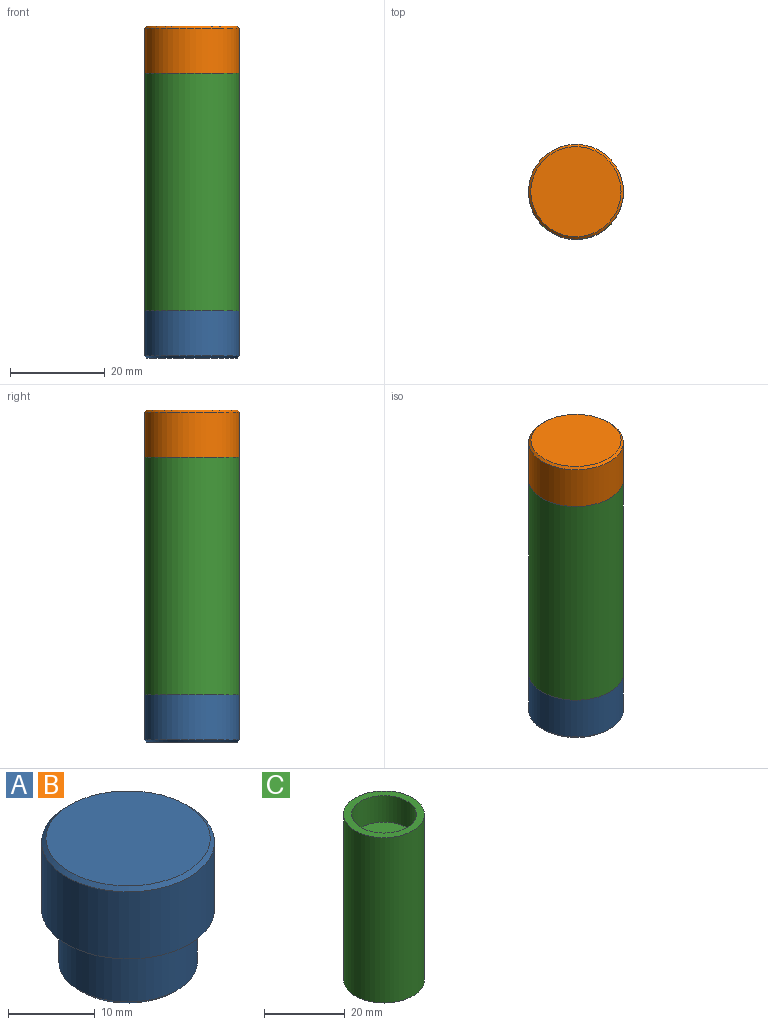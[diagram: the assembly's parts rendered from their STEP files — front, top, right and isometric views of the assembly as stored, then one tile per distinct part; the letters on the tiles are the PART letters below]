
ASSEMBLY  parts=3 mates=2
PART A: 7 faces, bbox 20x20x18 mm
  f0: cylinder r=10mm len=20mm, axis (0,0,-1), area 596.9mm2, adj f2,f6
  f1: plane 19x19mm, normal (0,0,1), area 283.5mm2, adj f6
  f2: plane 20x20mm, normal (0,0,-1), area 113.1mm2, adj f0,f3
  f3: cylinder r=8mm len=16mm, axis (0,0,1), area 377mm2, adj f2,f5
  f4: plane 15x15mm, normal (0,0,-1), area 176.7mm2, adj f5
  f5: cone r=8mm half-angle=45deg, axis (0,0,1), area 34.4mm2, adj f3,f4
  f6: cone r=9.5mm half-angle=45deg, axis (0,0,-1), area 43.3mm2, adj f0,f1
PART B: same geometry as A
PART C: 8 faces, bbox 20x20x50 mm
  f0: cylinder r=2mm len=7mm, axis (0,0,-1), area 88mm2, adj f5,f7
  f1: cylinder r=10mm len=50mm, axis (0,0,-1), area 3141.6mm2, adj f2,f3
  f2: plane 20x20mm, normal (0,0,1), area 113.1mm2, adj f1,f4
  f3: plane 20x20mm, normal (0,0,-1), area 113.1mm2, adj f1,f6
  f4: cylinder r=8mm len=16mm, axis (0,0,1), area 402.1mm2, adj f2,f5
  f5: plane 16x16mm, normal (0,0,1), area 188.5mm2, adj f0,f4
  f6: cylinder r=8mm len=35mm, axis (0,0,-1), area 1759.3mm2, adj f3,f7
  f7: plane 16x16mm, normal (0,0,-1), area 188.5mm2, adj f0,f6
PLACE A rot(axis=(1,0,0),180deg) t=(0,0,0)mm
PLACE B t=(0,0,50)mm
PLACE C at identity
MATE fastened A.f0 <-> C.f1  axis (0,0,1) through (0,0,0)mm
MATE fastened B.f3 <-> C.f1  axis (0,0,1) through (0,0,50)mm
